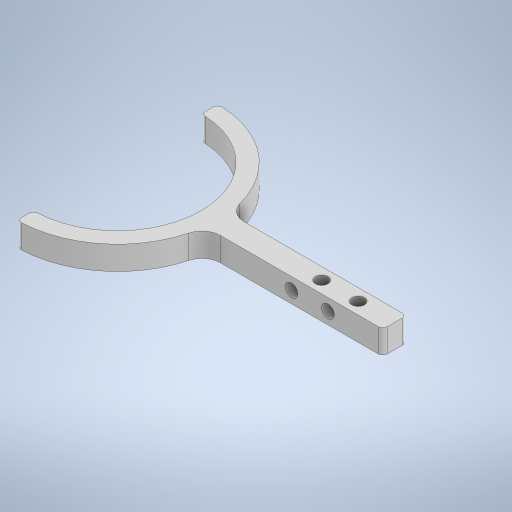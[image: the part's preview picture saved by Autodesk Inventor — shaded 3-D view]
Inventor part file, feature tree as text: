
AUTODESK INVENTOR PART (.ipt)
format: ipt  version: 2024.2 (Build 282272000, 272)  size: 285,696 bytes
history: native  units: mm
features: extrude x2, fillet x2, sketch x2, other x1, projected_geometry x1
ambient origin geometry x8: Origin, YZ Plane, XZ Plane, XY Plane, X Axis, Y Axis, Z Axis, Center Point
bodies: Body1 (feature_tree)
feature tree (8):
  other  "Bryła1"
  extrude  "Wyciągnięcie proste1"  Depth=46.0mm
  extrude  "Wyciągnięcie proste2"  Depth=4.5mm
  fillet  "Zaokrąglenie1"  Radius=4.5mm
  fillet  "Zaokrąglenie2"  Radius=6.5mm
  sketch  "Szkic1"
  sketch  "Szkic2"
  projected_geometry  "Pętla rzutowana1"
